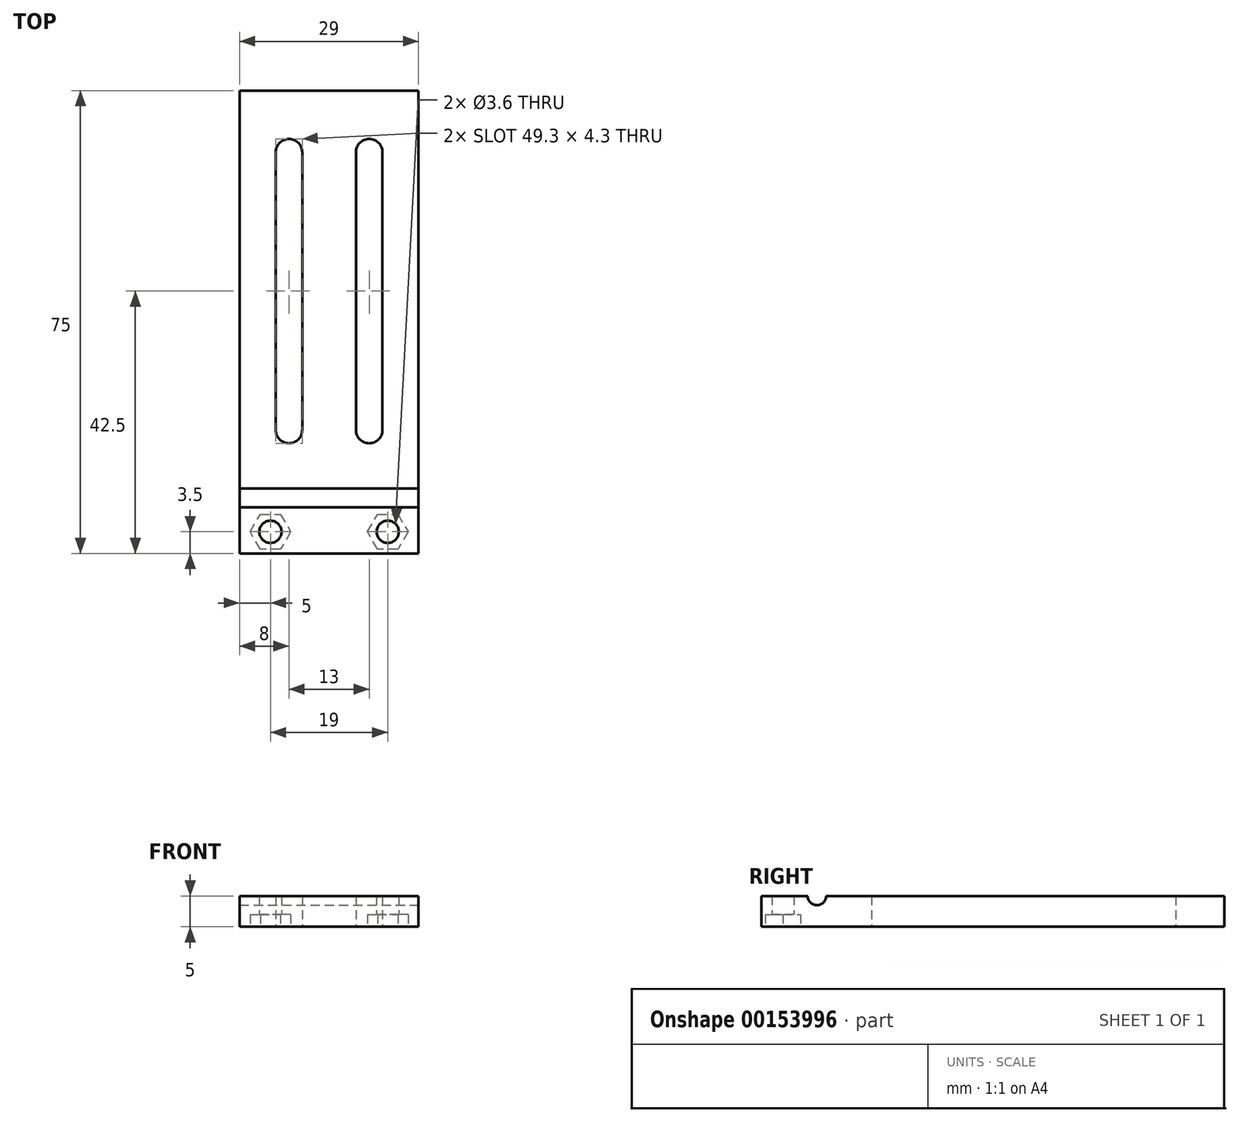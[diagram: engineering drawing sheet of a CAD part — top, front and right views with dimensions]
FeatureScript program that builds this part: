
annotation { "Feature Type Name" : "Feature", "Feature Type Description" : "" }
export const myFeature = defineFeature(function(context is Context, id is Id, definition is map)
    precondition{}
    {
        {
            var Q0;
            Q0=qCreatedBy(makeId("Top.planeOp"),FACE);
            var sketch = newSketch(context, id + "F0", { "sketchPlane" : qUnion([Q0])});
            skLineSegment(sketch, "E0.bottom", {"start": v(0, 0) * mm, "end": v(29, 0) * mm});
            skLineSegment(sketch, "E0.top", {"start": v(0, -75) * mm, "end": v(29, -75) * mm});
            skLineSegment(sketch, "E0.left", {"start": v(0, 0) * mm, "end": v(0, -75) * mm});
            skLineSegment(sketch, "E0.right", {"start": v(29, 0) * mm, "end": v(29, -75) * mm});
            skCircle(sketch, "E1", {"center": v(5, -71.5) * mm, "radius": 1.8 * mm});
            skCircle(sketch, "E2", {"center": v(24, -71.5) * mm, "radius": 1.8 * mm});
            skCircle(sketch, "E3", {"center": v(8, -10) * mm, "radius": 2.15 * mm, "construction": true});
            skCircle(sketch, "E4", {"center": v(21, -10) * mm, "radius": 2.15 * mm, "construction": true});
            skCircle(sketch, "E5", {"center": v(8, -55) * mm, "radius": 2.15 * mm, "construction": true});
            skCircle(sketch, "E6", {"center": v(21, -55) * mm, "radius": 2.15 * mm, "construction": true});
            skLineSegment(sketch, "E7", {"start": v(5.85, -10) * mm, "end": v(5.85, -55) * mm});
            skLineSegment(sketch, "E8", {"start": v(10.15, -10) * mm, "end": v(10.15, -55) * mm});
            skLineSegment(sketch, "E9", {"start": v(18.85, -10) * mm, "end": v(18.85, -55) * mm});
            skLineSegment(sketch, "E10", {"start": v(23.15, -10) * mm, "end": v(23.15, -55) * mm});
            skArc(sketch, "E11", {"start": v(5.85, -10) * mm, "mid": v(8, -7.85) * mm, "end": v(10.15, -10) * mm});
            skArc(sketch, "E12", {"start": v(18.85, -10) * mm, "mid": v(21, -7.85) * mm, "end": v(23.15, -10) * mm});
            skArc(sketch, "E13", {"start": v(23.15, -55) * mm, "mid": v(21, -57.15) * mm, "end": v(18.85, -55) * mm});
            skArc(sketch, "E14", {"start": v(10.15, -55) * mm, "mid": v(8, -57.15) * mm, "end": v(5.85, -55) * mm});
            skCircle(sketch, "E15.cCircle", {"center": v(5, -71.5) * mm, "radius": 2.85 * mm, "construction": true});
            skLineSegment(sketch, "E15.0", {"start": v(3.35, -68.65) * mm, "end": v(6.65, -68.65) * mm});
            skLineSegment(sketch, "E15.1", {"start": v(6.65, -68.65) * mm, "end": v(8.3, -71.5) * mm});
            skLineSegment(sketch, "E15.2", {"start": v(8.3, -71.5) * mm, "end": v(6.65, -74.35) * mm});
            skLineSegment(sketch, "E15.3", {"start": v(6.65, -74.35) * mm, "end": v(3.35, -74.35) * mm});
            skLineSegment(sketch, "E15.4", {"start": v(3.35, -74.35) * mm, "end": v(1.7, -71.5) * mm});
            skLineSegment(sketch, "E15.5", {"start": v(1.7, -71.5) * mm, "end": v(3.35, -68.65) * mm});
            skPoint(sketch, "E15.0.midPoint", {"position": v(5, -68.65) * mm});
            skCircle(sketch, "E16.cCircle", {"center": v(24, -71.5) * mm, "radius": 2.85 * mm, "construction": true});
            skLineSegment(sketch, "E16.0", {"start": v(22.35, -68.65) * mm, "end": v(25.65, -68.65) * mm});
            skLineSegment(sketch, "E16.1", {"start": v(25.65, -68.65) * mm, "end": v(27.3, -71.5) * mm});
            skLineSegment(sketch, "E16.2", {"start": v(27.3, -71.5) * mm, "end": v(25.65, -74.35) * mm});
            skLineSegment(sketch, "E16.3", {"start": v(25.65, -74.35) * mm, "end": v(22.35, -74.35) * mm});
            skLineSegment(sketch, "E16.4", {"start": v(22.35, -74.35) * mm, "end": v(20.7, -71.5) * mm});
            skLineSegment(sketch, "E16.5", {"start": v(20.7, -71.5) * mm, "end": v(22.35, -68.65) * mm});
            skPoint(sketch, "E16.0.midPoint", {"position": v(24, -68.65) * mm});
            skSolve(sketch);
        }
        {
            var Q0;
            Q0=makeQuery(id+"F0.imprint","IMPRINT",FACE,{"disambiguationData":[TD([[makeQuery(id+"F0.imprint","IMPRINT",EDGE,{"derivedFrom":sQuery(id+"F0.wireOp",EDGE,"E0.bottom")}),-1.0]])]});
            var Q1;
            Q1=makeQuery(id+"F0.imprint","IMPRINT",FACE,{"disambiguationData":[TD([[makeQuery(id+"F0.imprint","IMPRINT",EDGE,{"derivedFrom":sQuery(id+"F0.wireOp",EDGE,"E2")}),-1.0]])]});
            var Q2;
            Q2=makeQuery(id+"F0.imprint","IMPRINT",FACE,{"disambiguationData":[TD([[makeQuery(id+"F0.imprint","IMPRINT",EDGE,{"derivedFrom":sQuery(id+"F0.wireOp",EDGE,"E1")}),-1.0]])]});
            extrude(context, id + "F1", {"entities" : qUnion([Q0, Q1, Q2]), "depth" : 5 * mm});
        }
        {
            var Q0;
            Q0=makeQuery(id+"F1.opExtrude","SWEPT_FACE",FACE,{"disambiguationData":[OSD([sQuery(id+"F0.wireOp",EDGE,"E0.right")])]});
            var sketch = newSketch(context, id + "F2", { "sketchPlane" : qUnion([Q0])});
            skPoint(sketch, "E17.0", {"position": v(-71.5, 0) * mm});
            skLineSegment(sketch, "E18", {"start": v(-71.5, 0) * mm, "end": v(-71.5, 5) * mm, "construction": true});
            skArc(sketch, "E19", {"start": v(-67.5, 5) * mm, "mid": v(-66, 3.5) * mm, "end": v(-64.5, 5) * mm});
            skLineSegment(sketch, "E20", {"start": v(-75, 0) * mm, "end": v(-75, -1.5) * mm});
            skLineSegment(sketch, "E21", {"start": v(-75, -1.5) * mm, "end": v(-64.5, -1.5) * mm});
            skLineSegment(sketch, "E22", {"start": v(-64.5, -1.5) * mm, "end": v(-63, 0) * mm});
            skSolve(sketch);
        }
        {
            var Q0;
            Q0=qSketchRegion(id+"F2",true);
            var Q1;
            {var subQ0=sQuery(id+"F2.wireOp",EDGE,"E19");Q1=makeQuery(id+"F2.imprint","IMPRINT",FACE,{"disambiguationData":[TD([[makeQuery(id+"F2.imprint","IMPRINT",EDGE,{"derivedFrom":subQ0}),1.0]])]});}
            extrude(context, id + "F3", {"entities" : qUnion([Q0, Q1]), "operationType" : NewBodyOperationType.REMOVE, "endBound" : BoundingType.UP_TO_NEXT, "oppositeDirection" : true, "depth" : 25 * mm});
        }
        {
            var Q0;
            Q0=makeQuery(id+"F0.imprint","IMPRINT",FACE,{"disambiguationData":[TD([[makeQuery(id+"F0.imprint","IMPRINT",EDGE,{"derivedFrom":sQuery(id+"F0.wireOp",EDGE,"E1")}),1.0]])]});
            var Q1;
            Q1=makeQuery(id+"F0.imprint","IMPRINT",FACE,{"disambiguationData":[TD([[makeQuery(id+"F0.imprint","IMPRINT",EDGE,{"derivedFrom":sQuery(id+"F0.wireOp",EDGE,"E2")}),1.0]])]});
            var Q2;
            Q2=makeQuery(id+"F0.imprint","IMPRINT",FACE,{"disambiguationData":[TD([[makeQuery(id+"F0.imprint","IMPRINT",EDGE,{"derivedFrom":sQuery(id+"F0.wireOp",EDGE,"E1")}),-1.0]])]});
            var Q3;
            Q3=makeQuery(id+"F0.imprint","IMPRINT",FACE,{"disambiguationData":[TD([[makeQuery(id+"F0.imprint","IMPRINT",EDGE,{"derivedFrom":sQuery(id+"F0.wireOp",EDGE,"E2")}),-1.0]])]});
            extrude(context, id + "F4", {"entities" : qUnion([Q0, Q1, Q2, Q3]), "operationType" : NewBodyOperationType.REMOVE, "depth" : 2 * mm});
        }
    });
